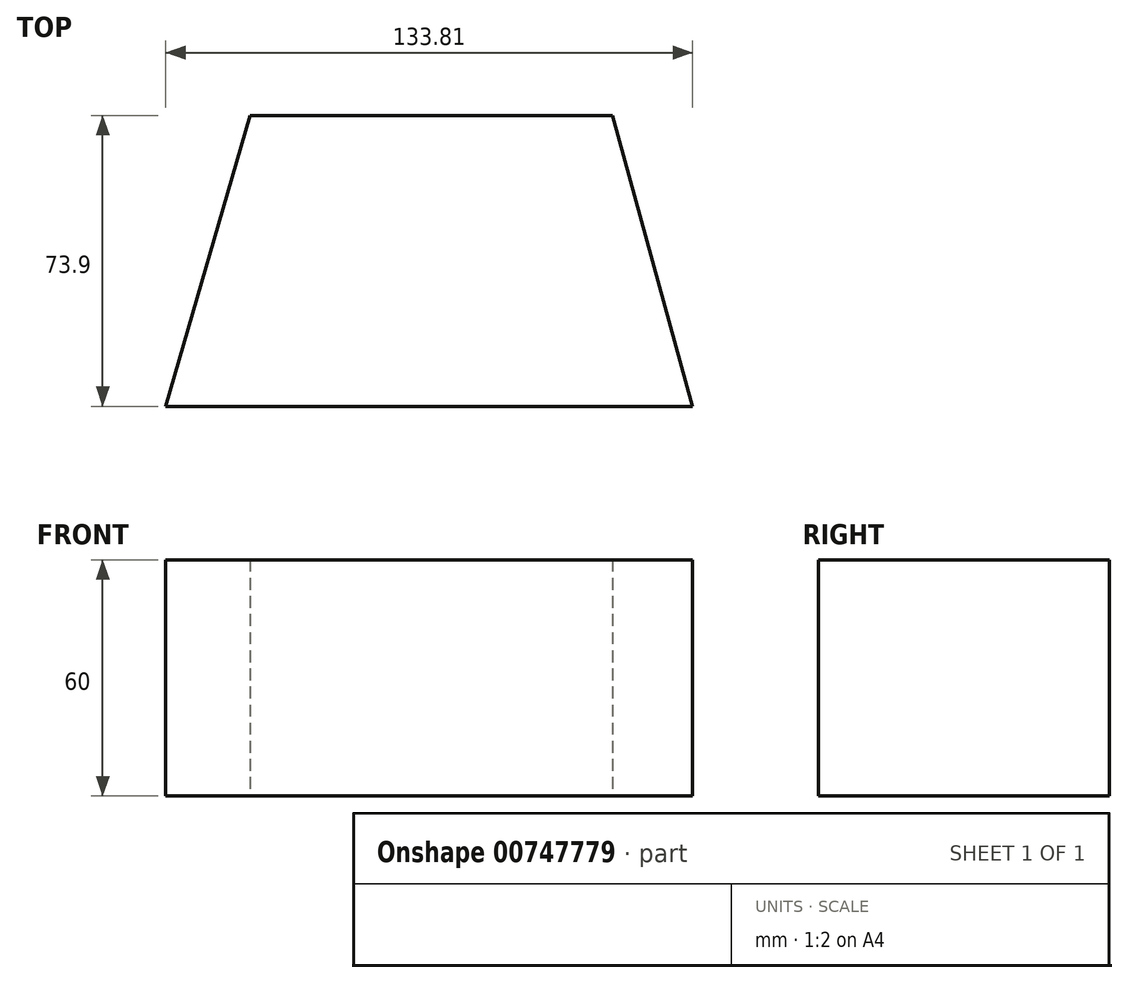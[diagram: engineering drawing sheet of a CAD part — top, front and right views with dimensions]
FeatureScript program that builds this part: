
annotation { "Feature Type Name" : "Feature", "Feature Type Description" : "" }
export const myFeature = defineFeature(function(context is Context, id is Id, definition is map)
    precondition{}
    {
        {
            var Q0;
            Q0=qCreatedBy(makeId("Top.planeOp"),FACE);
            var sketch = newSketch(context, id + "F0", { "sketchPlane" : qUnion([Q0])});
            skLineSegment(sketch, "E0.bottom", {"start": v(-45.78, 34.4) * mm, "end": v(46.28, 34.4) * mm});
            skLineSegment(sketch, "E0.top", {"start": v(-67.24, -39.5) * mm, "end": v(66.57, -39.5) * mm});
            skLineSegment(sketch, "E1", {"start": v(-67.24, -39.5) * mm, "end": v(-45.78, 34.4) * mm});
            skLineSegment(sketch, "E2", {"start": v(66.57, -39.5) * mm, "end": v(46.28, 34.4) * mm});
            skSolve(sketch);
        }
        {
            var Q0;
            {var subQ0=sQuery(id+"F0.wireOp",EDGE,"E0.left");Q0=makeQuery(id+"F0.imprint","IMPRINT",FACE,{"disambiguationData":[TD([[makeQuery(id+"F0.imprint","IMPRINT",EDGE,{"derivedFrom":subQ0}),1.0]])]});}
            var Q1;
            Q1=makeQuery(id+"F0.imprint","IMPRINT",FACE,{"disambiguationData":[TD([[makeQuery(id+"F0.imprint","IMPRINT",EDGE,{"derivedFrom":sQuery(id+"F0.wireOp",EDGE,"E0.top")}),1.0]])]});
            extrude(context, id + "F1", {"entities" : qUnion([Q0, Q1]), "endBound" : BoundingType.SYMMETRIC, "depth" : 60 * mm, "offsetDistance" : 25.4 * mm});
        }
    });
